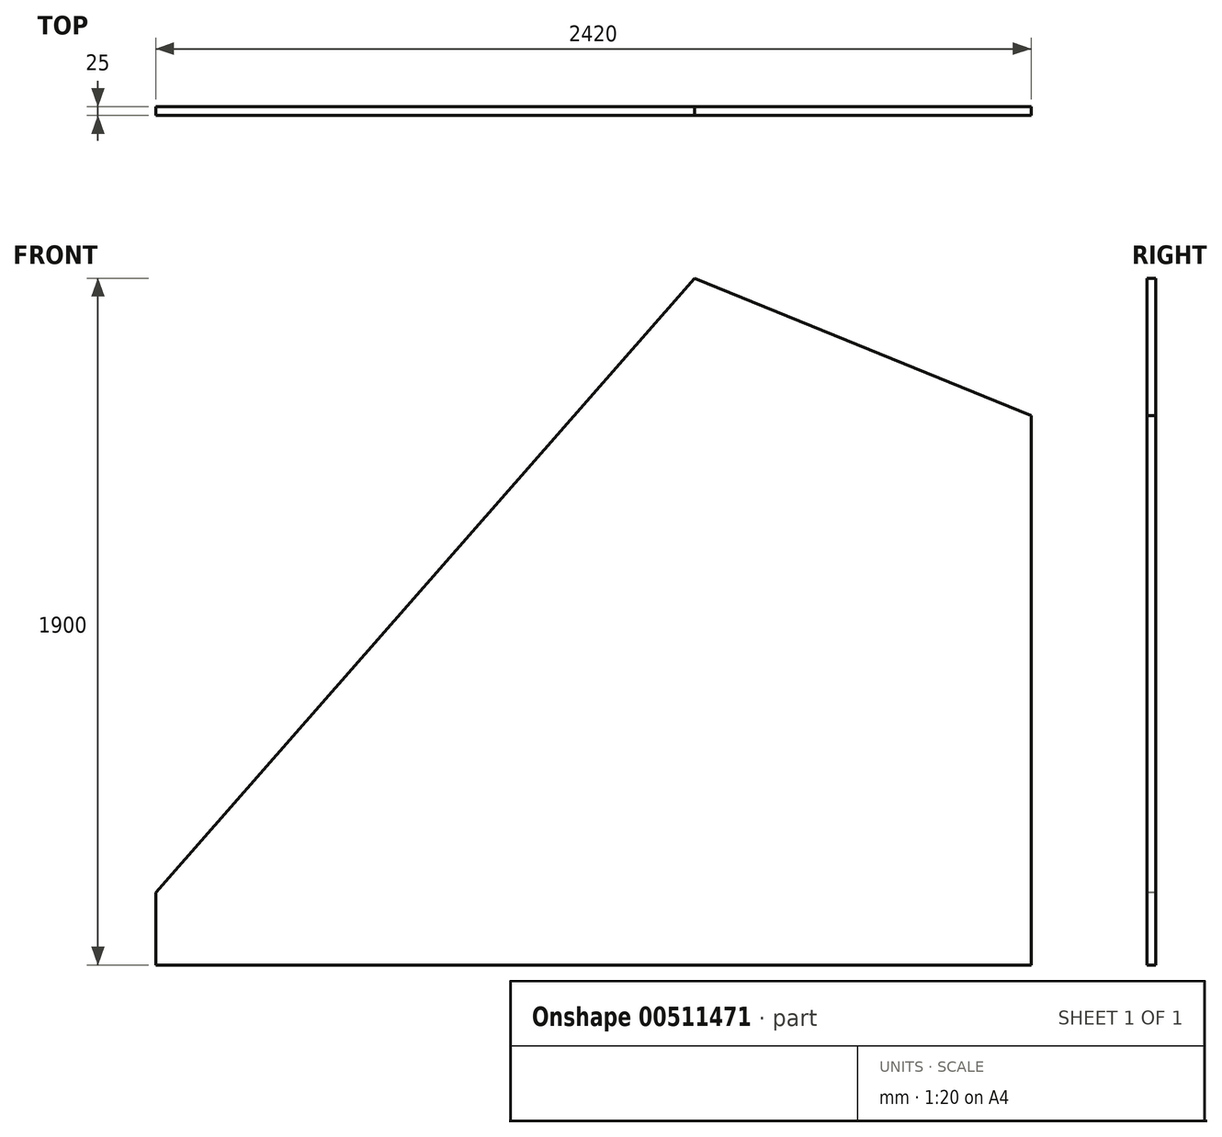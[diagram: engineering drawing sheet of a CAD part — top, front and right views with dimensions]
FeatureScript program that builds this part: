
annotation { "Feature Type Name" : "Feature", "Feature Type Description" : "" }
export const myFeature = defineFeature(function(context is Context, id is Id, definition is map)
    precondition{}
    {
        {
            var Q0;
            Q0=qCreatedBy(makeId("Front.planeOp"),FACE);
            var sketch = newSketch(context, id + "F0", { "sketchPlane" : qUnion([Q0])});
            skLineSegment(sketch, "E0", {"start": v(0, 0) * mm, "end": v(-2420, 0) * mm});
            skLineSegment(sketch, "E1", {"start": v(-2420, 0) * mm, "end": v(-2420, 200) * mm});
            skLineSegment(sketch, "E2", {"start": v(-2420, 200) * mm, "end": v(-930, 1900) * mm});
            skLineSegment(sketch, "E3", {"start": v(-930, 1900) * mm, "end": v(0, 1520) * mm});
            skLineSegment(sketch, "E4", {"start": v(0, 1520) * mm, "end": v(0, 0) * mm});
            skLineSegment(sketch, "E5", {"start": v(-930, 1900) * mm, "end": v(-930, 0) * mm, "construction": true});
            skSolve(sketch);
        }
        {
            var Q0;
            Q0 = qSketchRegion(id + "F0", true);
            extrude(context, id + "F1", {"entities" : qUnion([Q0]), "oppositeDirection" : true, "depth" : 25 * mm});
        }
    });
